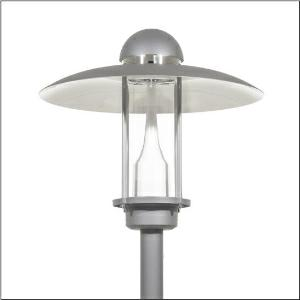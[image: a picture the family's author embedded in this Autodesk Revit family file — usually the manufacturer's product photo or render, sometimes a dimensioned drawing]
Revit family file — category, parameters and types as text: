
# Revit family: city-light_elegance_iq___p1_0a_5xa5265bf14h_371a
name_source: partatom
category: Lighting Fixtures
units: mm (PartAtom-declared; Revit-internal decimal feet)

## family parameters
Cut with Voids When Loaded = No
Host = Face
Light Source = No
Part Type = Normal
Room Calculation Point = No
Round Connector Dimension = Use Diameter
Shared = No

## types (1)
- --- (1 x LED, 1440 lm, 12.9 W, 2200K)
    Apparent Load = 13 VA
    CIE Flux Codes = 32 62 91 97 100
    Color Rendering = 70
    Color Temperature = 2200K
    Default Elevation = 1800 mm
    Description = City-Light Elegance iQ, mast luminaire, Module 540 iQ-SR, primary light control with 3 zone facetted reflector, of plastic, silver coated, highly specular, structured, primary optical cover: cover, of PMMA, transparent, light distribution: P1.0a, light emission: direct distribution, primary light characteristic: strongly asymmetric, installation type: post-top, LED, High Power LED, rated luminous flux: 1.440lm, luminous efficacy: 112lm/W, light colour: 722, colour temperature: 2200K, control gear: ECG iQ, control: presetting dimming logarithmic, Street-Remote, Auto-Match, Temp-Guard, Lumen-Switch, Night-Set, Smart-Wire, Light-Fading, Desk-Remote (wireless, voltage-free reading and setting of iQ features in the workshop via application-optimized NFC function/RFID function), optimised constant luminous flux control (CLO 2.0), with terminal, 6-pole, max. 2.5mm², mains connection: 230..240V, AC, 50/60Hz, start of lifetime: 13W, end of service life: 13W, reduction: 6W, luminaire housing, upper part, of aluminium, coated, Siteco® metallic grey (DB 702S), diameter: 750mm, height: 675mm, spigot size: d x l = 76 x 70mm (post-top) | with reducer (optional accessory) 60 x 70mm, post-top mast mounting element, of diecast aluminium, coated, Siteco® metallic grey (DB 702S), Module 540 iQ-SR, traffic white (RAL 9016), equipment: standard, protection rating (complete): IP65, insulation class (complete): insulation class II (safety insulation), certification: CE, ENEC, VDE, packaging unit: 1 piece

Light Distribution: P1.0a
    Height = 675 mm
    Lamp = 1 x LED
    Lamp Light Flux = 1440 lm
    Lamp Power = 12.9 W
    Lamp count = 1
    Length = 750 mm
    Luminous efficacy = 112 lm/W
    Manufacturer = Siteco
    ModVariant = No
    Model = 5XA5265BF14H
    Number of Poles = 1
    OnlyDefault = Yes
    Power Factor = 1
    Product Name = City-Light Elegance iQ | P1.0a
    Product group = mast luminaire | pylon top
    ProductGroupID = 6100
    Protection Class = Protection class II
    Protection Degree = IP 65
    RLX_Detail_Level = 1
    RLX_Emergency_Light_Flux = 0 lm
    RLX_Emergency_Type = 0
    RLX_Emergency_Type_DB = No
    RlxData = <blob elided: 102009 chars, md5=74968104>
    Socket = socket
    Standby Power = 0 W
    System Light Flux = 1440 lm
    System Power = 13 W
    Type Comments = factory setting: luminous flux: 100 % | dim-lin: 254 | 516 mA
    Type Image = l_1006912.jpg
    URL = http://relux.com
    VarID = @adj_109933
    Voltage = 0 V
    Weight = 0.00 kg
    Width = 0 mm  [stored 0 ft]

note: [stored X ft] marks values corroborated as IEEE doubles in the binary element streams (Revit-internal decimal feet)

## geometry (parser evidence)
native form markers: Blend x4, Sweep x12
no freeform markers — native parametric forms only
